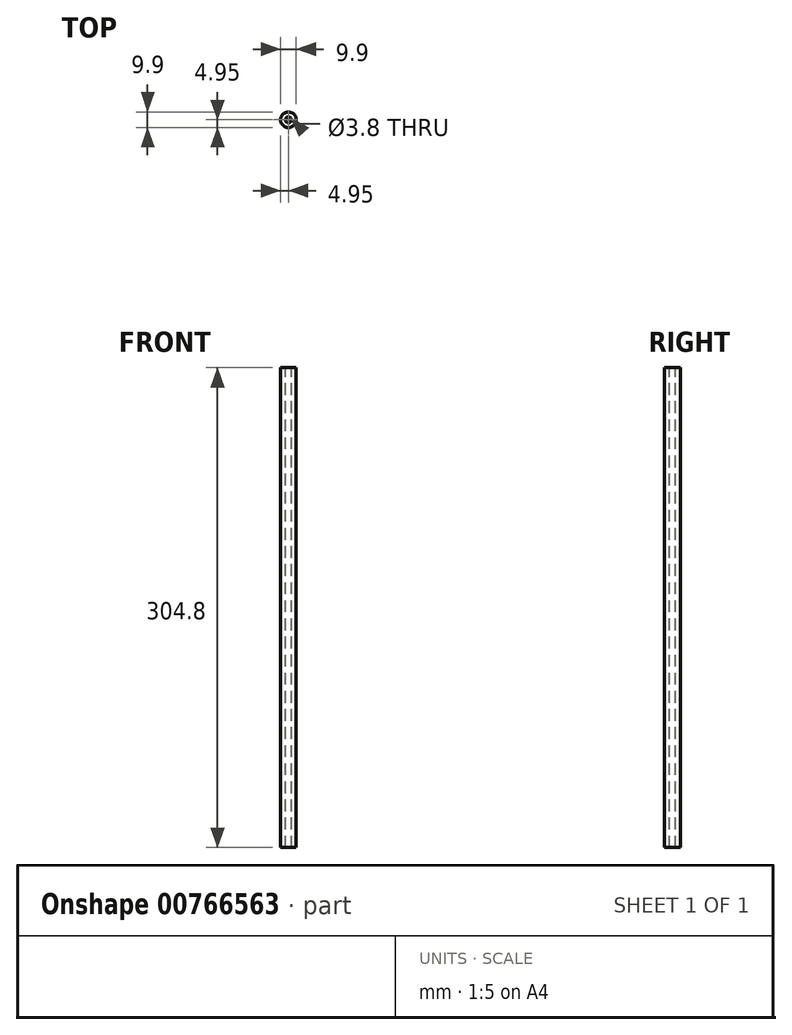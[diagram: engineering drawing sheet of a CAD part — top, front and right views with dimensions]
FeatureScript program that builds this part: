
annotation { "Feature Type Name" : "Feature", "Feature Type Description" : "" }
export const myFeature = defineFeature(function(context is Context, id is Id, definition is map)
    precondition{}
    {
        {
            var Q0;
            Q0=qCreatedBy(makeId("Top.planeOp"),FACE);
            var sketch = newSketch(context, id + "F0", { "sketchPlane" : qUnion([Q0])});
            skCircle(sketch, "E0", {"center": v(0, 0) * mm, "radius": 4.95 * mm});
            skSolve(sketch);
        }
        {
            var Q0;
            Q0 = qSketchRegion(id + "F0", true);
            extrude(context, id + "F1", {"entities" : qUnion([Q0]), "depth" : 304.8 * mm, "offsetDistance" : 25.4 * mm});
        }
        {
            var Q0;
            Q0=makeQuery(id+"F1.opExtrude","CAP_FACE",FACE,{"disambiguationData":[OSD([sQuery(id+"F0.wireOp",EDGE,"E0")])],"isStart":false});
            var sketch = newSketch(context, id + "F2", { "sketchPlane" : qUnion([Q0])});
            skPoint(sketch, "E1", {"position": v(0, 0) * mm});
            skPoint(sketch, "E2", {"position": v(-120.36, 9.3) * mm});
            skSolve(sketch);
        }
        {
            var Q0;
            Q0=sQuery(id+"F2.wireOp",VERTEX,"E1");
            var Q1;
            Q1=makeQuery(id+"F1.opExtrude","SWEPT_BODY",BODY,{"disambiguationData":[OSD([sQuery(id+"F0.wireOp",EDGE,"E0")])]});
            hole(context, id + "F3", {"style" : HoleStyle.SIMPLE, "endStyle" : HoleEndStyle.THROUGH, "standardTappedOrClearance" : lookupTablePath({ "standard" : "ANSI", "engagement" : "75%", "pitch" : "24 tpi", "size" : "#10", "type" : "Tapped" }), "standardBlindInLast" : lookupTablePath({ "standard" : "ANSI", "engagement" : "75%", "pitch" : "24 tpi", "size" : "#10", "type" : "Tapped" }), "holeDiameter" : 3.8 * mm, "majorDiameter" : 4.83 * mm, "showTappedDepth" : true, "isTappedThrough" : true, "tappedDepth" : 12.7 * mm, "tapClearance" : 3, "locations" : qUnion([Q0]), "scope" : qUnion([Q1])});
        }
    });
